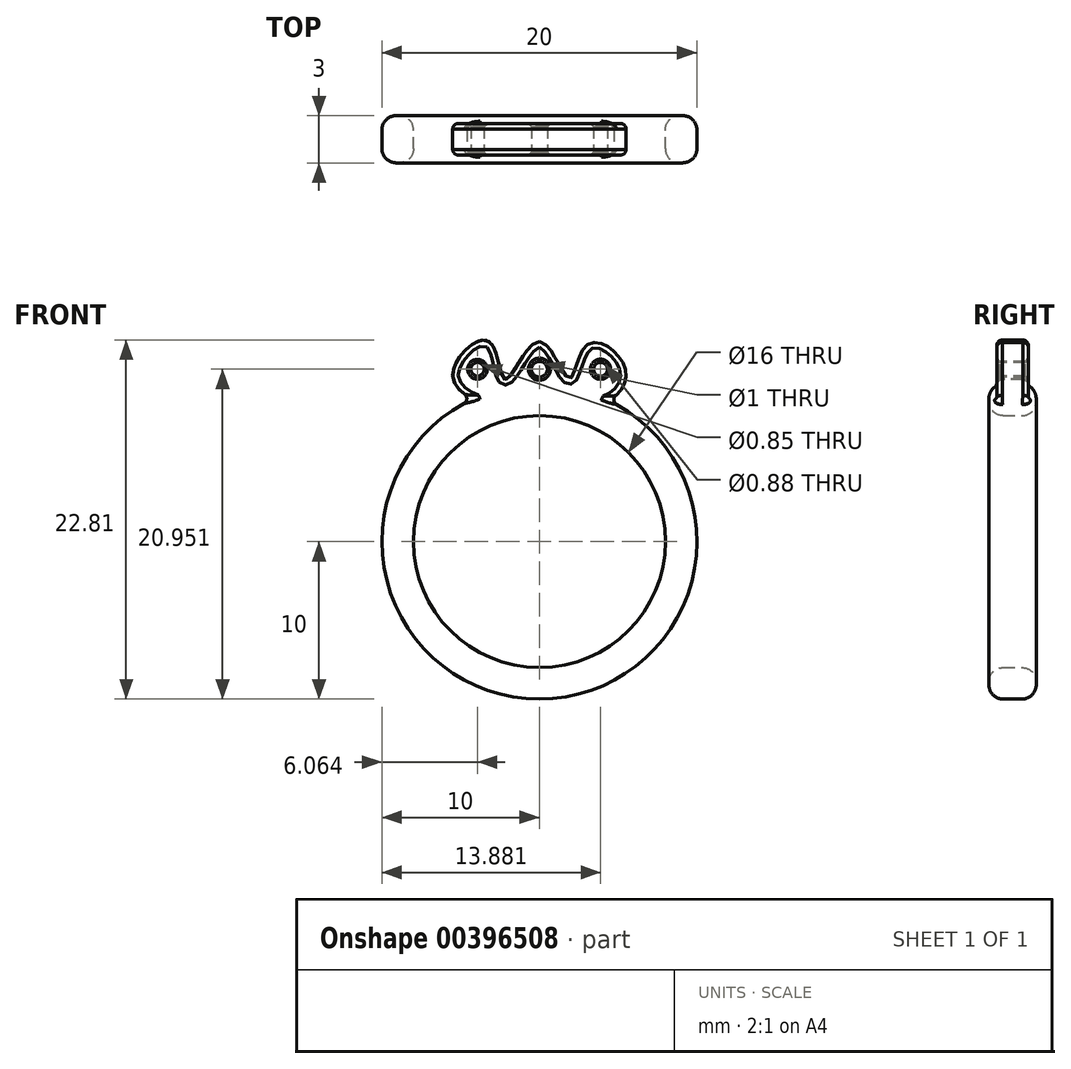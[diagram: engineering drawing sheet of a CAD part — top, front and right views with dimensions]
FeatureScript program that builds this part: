
annotation { "Feature Type Name" : "Feature", "Feature Type Description" : "" }
export const myFeature = defineFeature(function(context is Context, id is Id, definition is map)
    precondition{}
    {
        {
            var Q0;
            Q0=qCreatedBy(makeId("Front.planeOp"),FACE);
            var sketch = newSketch(context, id + "F0", { "sketchPlane" : qUnion([Q0])});
            skCircle(sketch, "E0", {"center": v(0, 0) * mm, "radius": 8 * mm});
            skCircle(sketch, "E1", {"center": v(0, 0) * mm, "radius": 10 * mm});
            skSolve(sketch);
        }
        {
            var Q0;
            Q0=makeQuery(id+"F0.imprint","IMPRINT",FACE,{"disambiguationData":[TD([[makeQuery(id+"F0.imprint","IMPRINT",EDGE,{"derivedFrom":sQuery(id+"F0.wireOp",EDGE,"E0")}),-1.0]])]});
            extrude(context, id + "F1", {"entities" : qUnion([Q0]), "depth" : 3 * mm});
        }
        {
            var Q0;
            Q0=makeQuery(id+"F1.opExtrude","CAP_EDGE",EDGE,{"disambiguationData":[OSD([sQuery(id+"F0.wireOp",EDGE,"E1")])],"isStart":false});
            var Q1;
            Q1=makeQuery(id+"F1.opExtrude","CAP_EDGE",EDGE,{"disambiguationData":[OSD([sQuery(id+"F0.wireOp",EDGE,"E1")])],"isStart":true});
            var Q2;
            Q2=makeQuery(id+"F1.opExtrude","CAP_EDGE",EDGE,{"disambiguationData":[OSD([sQuery(id+"F0.wireOp",EDGE,"E0")])],"isStart":false});
            var Q3;
            Q3=makeQuery(id+"F1.opExtrude","CAP_EDGE",EDGE,{"disambiguationData":[OSD([sQuery(id+"F0.wireOp",EDGE,"E0")])],"isStart":true});
            fillet(context, id + "F2", {"entities" : qUnion([Q0, Q1, Q2, Q3]), "radius" : 0.9 * mm, "tangentPropagation" : true, "allowEdgeOverflow" : false});
        }
        {
            var Q0;
            Q0=qCreatedBy(makeId("Top.planeOp"),FACE);
            cPlane(context, id + "F3", {"entities" : qUnion([Q0]), "cplaneType" : CPlaneType.OFFSET, "offset" : 9 * mm, "width" : 150 * mm, "height" : 150 * mm});
        }
        {
            var Q0;
            Q0=qCreatedBy(id+"F3.planeOp",FACE);
            var sketch = newSketch(context, id + "F4", { "sketchPlane" : qUnion([Q0])});
            skLineSegment(sketch, "E2", {"start": v(9.1, -3) * mm, "end": v(-9.1, -3) * mm});
            skLineSegment(sketch, "E3", {"start": v(9.1, 0) * mm, "end": v(-9.1, 0) * mm});
            skCircle(sketch, "E4", {"center": v(0, -1.5) * mm, "radius": 1.05 * mm});
            skPoint(sketch, "E4.centerSnap0", {"position": v(0, -3) * mm});
            skSolve(sketch);
        }
        {
            var Q0;
            Q0=qCreatedBy(makeId("Front.planeOp"),FACE);
            var Q1;
            Q1=sQuery(id+"F4.wireOp",VERTEX,"E4.center");
            cPlane(context, id + "F5", {"entities" : qUnion([Q0, Q1]), "cplaneType" : CPlaneType.PLANE_POINT, "offset" : 25 * mm, "width" : 150 * mm, "height" : 150 * mm});
        }
        {
            var Q0;
            Q0=qCreatedBy(id+"F5.planeOp",FACE);
            var sketch = newSketch(context, id + "F6", { "sketchPlane" : qUnion([Q0])});
            skPoint(sketch, "E5.0", {"position": v(0, 9) * mm});
            skLineSegment(sketch, "E6", {"start": v(0, 9) * mm, "end": v(0, 12.7) * mm});
            skFitSpline(sketch, "E7", {"points": [v(0, 9) * mm, v(-2.8, 9) * mm, v(-4.02, 9) * mm, v(-5.5, 10.7) * mm, v(-3.22, 12.73) * mm, v(-2.17, 10.29) * mm, v(0, 12.7) * mm, v(1.89, 10.34) * mm, v(3.06, 12.53) * mm, v(5.41, 11.1) * mm, v(4.38, 9) * mm, v(1.38, 9) * mm, v(0, 9) * mm]});
            skSolve(sketch);
        }
        {
            var Q0;
            Q0 = qSketchRegion(id + "F6", true);
            extrude(context, id + "F7", {"entities" : qUnion([Q0]), "operationType" : NewBodyOperationType.ADD, "oppositeDirection" : true, "depth" : 2 * mm, "symmetric" : true});
        }
        {
            var Q0;
            Q0=makeQuery(id+"F7.opExtrude","CAP_FACE",FACE,{"disambiguationData":[OSD([sQuery(id+"F6.wireOp",EDGE,"E7")])],"isStart":false});
            var Q1;
            Q1=makeQuery(id+"F7.opExtrude","CAP_FACE",FACE,{"disambiguationData":[OSD([sQuery(id+"F6.wireOp",EDGE,"E7")])],"isStart":true});
            var Q2;
            Q2=makeQuery(id+"F7.opExtrude","SWEPT_FACE",FACE,{"disambiguationData":[OSD([sQuery(id+"F6.wireOp",EDGE,"E7")])]});
            fillet(context, id + "F8", {"entities" : qUnion([Q0, Q1, Q2]), "radius" : 0.35 * mm, "tangentPropagation" : true, "allowEdgeOverflow" : false});
        }
        {
            var Q0;
            Q0=makeQuery(id+"F7.opExtrude","CAP_FACE",FACE,{"disambiguationData":[OSD([sQuery(id+"F6.wireOp",EDGE,"E7")])],"isStart":true});
            var sketch = newSketch(context, id + "F9", { "sketchPlane" : qUnion([Q0])});
            skCircle(sketch, "E8", {"center": v(0, 10.95) * mm, "radius": 0.5 * mm});
            skCircle(sketch, "E9", {"center": v(-3.94, 10.95) * mm, "radius": 0.42 * mm});
            skCircle(sketch, "E10", {"center": v(3.88, 10.95) * mm, "radius": 0.44 * mm});
            skLineSegment(sketch, "E11", {"start": v(-7.04, 10.95) * mm, "end": v(7.82, 10.95) * mm, "construction": true});
            skSolve(sketch);
        }
        {
            var Q0;
            Q0 = qSketchRegion(id + "F9", true);
            extrude(context, id + "F10", {"entities" : qUnion([Q0]), "operationType" : NewBodyOperationType.REMOVE, "oppositeDirection" : true, "depth" : 25 * mm});
        }
        {
            var Q0;
            Q0=makeQuery(id+"F10.boolean.opBoolean","COPY",FACE,{"derivedFrom":makeQuery(id+"F10.opExtrude","SWEPT_FACE",FACE,{"disambiguationData":[OSD([sQuery(id+"F9.wireOp",EDGE,"E9")])]})});
            var Q1;
            Q1=makeQuery(id+"F10.boolean.opBoolean","COPY",FACE,{"derivedFrom":makeQuery(id+"F10.opExtrude","SWEPT_FACE",FACE,{"disambiguationData":[OSD([sQuery(id+"F9.wireOp",EDGE,"E8")])]})});
            var Q2;
            Q2=makeQuery(id+"F10.boolean.opBoolean","COPY",FACE,{"derivedFrom":makeQuery(id+"F10.opExtrude","SWEPT_FACE",FACE,{"disambiguationData":[OSD([sQuery(id+"F9.wireOp",EDGE,"E10")])]})});
            chamfer(context, id + "F11", {"entities" : qUnion([Q0, Q1, Q2]), "width" : 0.2 * mm, "tangentPropagation" : true});
        }
    });
